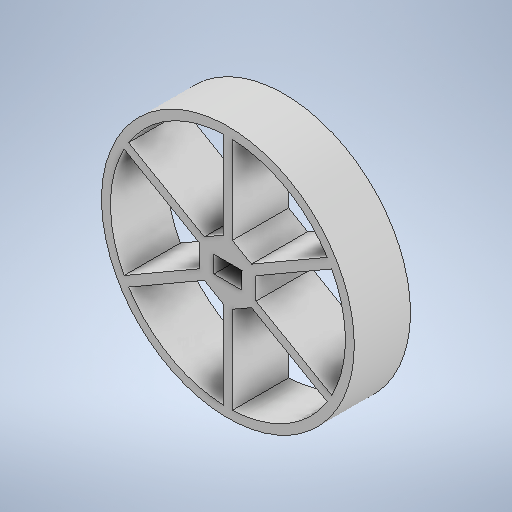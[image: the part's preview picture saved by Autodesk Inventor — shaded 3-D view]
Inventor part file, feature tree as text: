
AUTODESK INVENTOR PART (.ipt)
format: ipt  version: 2025.3 (Build 293356030, 356C)  size: 287,232 bytes
history: native  units: mm
features: sketch x3, extrude x2, other x1, pattern_circular x1
ambient origin geometry x8: Origin, YZ Plane, XZ Plane, XY Plane, X Axis, Y Axis, Z Axis, Center Point
bodies: Body1 (feature_tree)
feature tree (7):
  other  "ソリッド1"
  extrude  "スポーク"  Depth=10.0mm TaperAngle=0.0deg
  pattern_circular  "円形状パターン1"  [2 undecoded]
  extrude  "押し出し3"  Depth=60.0mm TaperAngle=360.0deg
  sketch  "スケッチ1"
  sketch  "スケッチ2"
  sketch  "スケッチ3"
note: 2 required parameter values undecoded (feature->parameter linkage not recoverable at this tier; creation-order binding heuristic only, values carry confidence <= 0.55)
